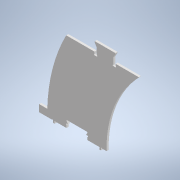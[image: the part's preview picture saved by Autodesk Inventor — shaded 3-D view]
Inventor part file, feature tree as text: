
AUTODESK INVENTOR PART (.ipt)
format: ipt  version: 2021 (Build 250183000, 183)  size: 378,880 bytes
history: native  units: mm
features: extrude x1, sketch x1
ambient origin geometry x8: Origin, YZ Plane, XZ Plane, XY Plane, X Axis, Y Axis, Z Axis, Center Point
bodies: Body1 (feature_tree)
feature tree (2):
  extrude  "Extrusion3"  Depth=53.623497mm
  sketch  "Sketch1"  dims[d13=550.0mm d17=200.0mm d18=0.0mm d19=150.0mm d54=220.0mm d56=220.0mm d57=30.0mm d73=236.680872mm d74=236.680872mm d75=576.435mm d76=472.393783mm d77=472.393783mm d78=30.0mm d81=220.0mm d82=252.393783mm d85=356.435mm d88=3.5mm d89=30.0mm d90=22.0mm d91=3.5mm d103=3.75mm d104=3.75mm d105=2.666667mm d106=30.0mm d107=20.0mm d108=2.666667mm d109=1.333333mm d110=7.333333mm d111=7.333333mm d112=7.5mm d113=3.75mm d114=3.75mm d134=3.5mm d135=65.0mm d136=65.0mm d137=7.333333mm d138=60.0deg d139=5.0mm d140=7.5mm d148=1.75mm d151=40.0mm d152=74.50599mm d153=20.666667mm d154=3.5mm d155=189.01198mm d159=1.75mm d160=1.75mm d161=1.75mm d164=7.5mm d168=21.25mm d170=30.0mm d171=1.75mm d172=10.0mm d173=3.5mm d177=3.5mm d178=65.0mm d179=65.0mm d180=7.333333mm d181=60.0deg d182=5.0mm d183=7.5mm d184=30.0mm d185=1.75mm d186=10.0mm d192=1.75mm d206=1.75mm d208=220.0mm d209=3.5mm d210=65.0mm d211=65.0mm d212=7.333333mm d213=60.0deg d214=5.0mm d215=7.5mm d216=30.0mm d217=1.75mm d218=10.0mm d219=7.0mm d220=1.75mm d222=23.0mm d226=1.75mm d228=53.623497mm d231=1.75mm d232=1.75mm d233=7.0mm d234=1.75mm d235=23.0mm d236=1.75mm d237=252.393783mm d240=3.0mm d241=3.5mm d242=8.0mm d243=1.75mm d244=1.75mm d245=7.0mm d246=1.75mm d247=23.0mm d248=1.75mm d249=220.0mm d261=3.0mm d263=7.0mm d264=0.0mm d265=0.0mm d274=3.5mm d275=65.0mm d276=65.0mm d277=7.333333mm d278=60.0deg d279=5.0mm d280=7.5mm d281=1.75mm d282=53.623497mm d284=374.457004mm d285=525.457594mm d286=0.865mm]
